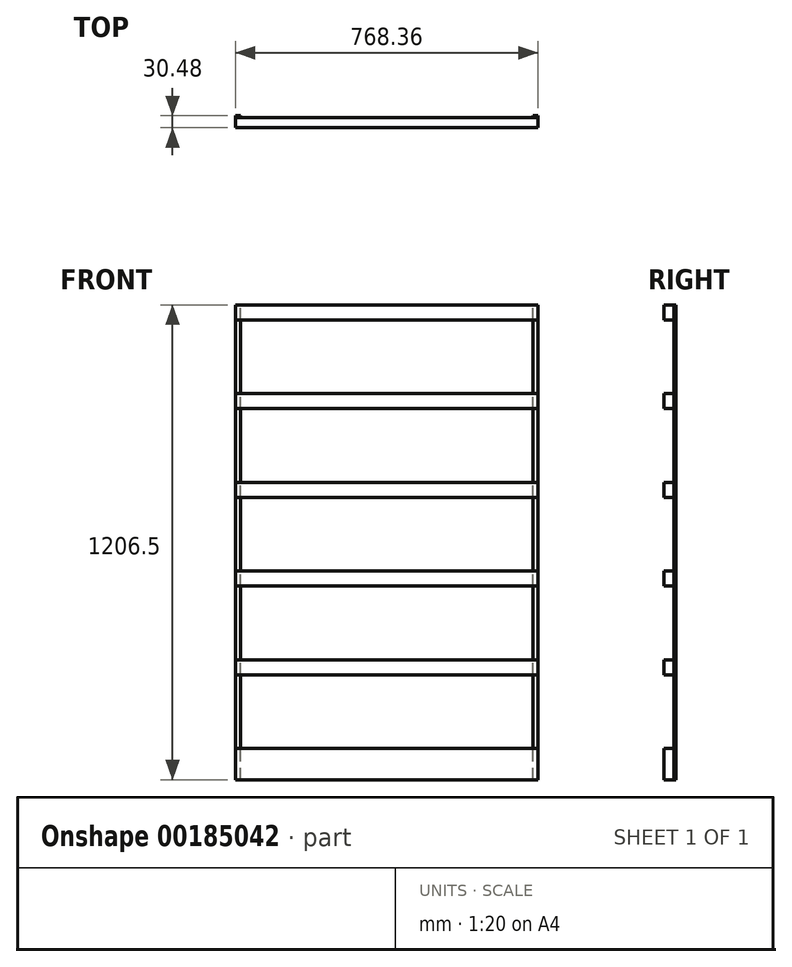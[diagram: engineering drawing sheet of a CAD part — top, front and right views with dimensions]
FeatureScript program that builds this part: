
annotation { "Feature Type Name" : "Feature", "Feature Type Description" : "" }
export const myFeature = defineFeature(function(context is Context, id is Id, definition is map)
    precondition{}
    {
        {
            var Q0;
            Q0=qCreatedBy(makeId("Front.planeOp"),FACE);
            var sketch = newSketch(context, id + "F0", { "sketchPlane" : qUnion([Q0])});
            skLineSegment(sketch, "E0.bottom", {"start": v(384.18, 603.25) * mm, "end": v(-384.18, 603.25) * mm});
            skLineSegment(sketch, "E0.top", {"start": v(384.18, -603.25) * mm, "end": v(-384.17, -603.25) * mm});
            skLineSegment(sketch, "E0.left", {"start": v(384.18, 603.25) * mm, "end": v(384.18, -603.25) * mm});
            skLineSegment(sketch, "E0.right", {"start": v(-384.18, 603.25) * mm, "end": v(-384.17, -603.25) * mm});
            skPoint(sketch, "E0.middle", {"position": v(0, 0) * mm});
            skSolve(sketch);
        }
        {
            var Q0;
            Q0 = qSketchRegion(id + "F0", true);
            extrude(context, id + "F1", {"entities" : qUnion([Q0]), "depth" : 25.4 * mm});
        }
        {
            var Q0;
            Q0=makeQuery(id+"F1.opExtrude","CAP_FACE",FACE,{"disambiguationData":[OSD([sQuery(id+"F0.wireOp",EDGE,"E0.bottom"),sQuery(id+"F0.wireOp",EDGE,"E0.top"),sQuery(id+"F0.wireOp",EDGE,"E0.left"),sQuery(id+"F0.wireOp",EDGE,"E0.right")])],"isStart":false});
            var sketch = newSketch(context, id + "F2", { "sketchPlane" : qUnion([Q0])});
            skLineSegment(sketch, "E1", {"start": v(-384.18, 565.15) * mm, "end": v(384.17, 565.15) * mm});
            skLineSegment(sketch, "E2", {"start": v(-384.18, 377.83) * mm, "end": v(384.18, 377.83) * mm});
            skLineSegment(sketch, "E3", {"start": v(-384.18, 339.73) * mm, "end": v(384.18, 339.73) * mm});
            skLineSegment(sketch, "E4", {"start": v(-384.18, 152.4) * mm, "end": v(384.18, 152.4) * mm});
            skLineSegment(sketch, "E5", {"start": v(-384.18, 114.3) * mm, "end": v(384.18, 114.3) * mm});
            skLineSegment(sketch, "E6", {"start": v(-384.18, -73.02) * mm, "end": v(384.18, -73.02) * mm});
            skLineSegment(sketch, "E7", {"start": v(-384.18, -111.12) * mm, "end": v(384.18, -111.12) * mm});
            skLineSegment(sketch, "E8", {"start": v(-384.17, -298.45) * mm, "end": v(384.18, -298.45) * mm});
            skLineSegment(sketch, "E9", {"start": v(-384.17, -336.55) * mm, "end": v(384.18, -336.55) * mm});
            skLineSegment(sketch, "E10", {"start": v(-384.17, -523.88) * mm, "end": v(384.18, -523.88) * mm});
            skLineSegment(sketch, "E11", {"start": v(-384.18, -336.55) * mm, "end": v(-384.17, -523.88) * mm});
            skLineSegment(sketch, "E12", {"start": v(384.18, -336.55) * mm, "end": v(384.18, -523.88) * mm});
            skLineSegment(sketch, "E13", {"start": v(384.18, -111.12) * mm, "end": v(384.18, -298.45) * mm});
            skLineSegment(sketch, "E14", {"start": v(-384.18, 565.15) * mm, "end": v(-384.18, 377.83) * mm});
            skLineSegment(sketch, "E15", {"start": v(384.17, 565.15) * mm, "end": v(384.18, 377.83) * mm});
            skLineSegment(sketch, "E16", {"start": v(384.18, 339.73) * mm, "end": v(384.18, 152.4) * mm});
            skLineSegment(sketch, "E17", {"start": v(-384.18, 339.73) * mm, "end": v(-384.18, 152.4) * mm});
            skLineSegment(sketch, "E18", {"start": v(-384.18, 114.3) * mm, "end": v(-384.18, -73.02) * mm});
            skSolve(sketch);
        }
        {
            var Q0;
            Q0 = qSketchRegion(id + "F2", true);
            var Q1;
            {var subQ0=sQuery(id+"F2.wireOp",EDGE,"E5");Q1=makeQuery(id+"F2.imprint","IMPRINT",FACE,{"disambiguationData":[TD([[makeQuery(id+"F2.imprint","IMPRINT",EDGE,{"derivedFrom":subQ0}),-1.0]])]});}
            var Q2;
            {var subQ0=sQuery(id+"F2.wireOp",EDGE,"E7");Q2=makeQuery(id+"F2.imprint","IMPRINT",FACE,{"disambiguationData":[TD([[makeQuery(id+"F2.imprint","IMPRINT",EDGE,{"derivedFrom":subQ0}),-1.0]])]});}
            extrude(context, id + "F3", {"entities" : qUnion([Q0, Q1, Q2]), "operationType" : NewBodyOperationType.REMOVE, "oppositeDirection" : true, "depth" : 25.4 * mm});
        }
        {
            var Q0;
            Q0=makeQuery(id+"F1.opExtrude","SWEPT_FACE",FACE,{"disambiguationData":[OSD([sQuery(id+"F0.wireOp",EDGE,"E0.bottom")])]});
            var sketch = newSketch(context, id + "F4", { "sketchPlane" : qUnion([Q0])});
            skLineSegment(sketch, "E19.bottom", {"start": v(-384.18, 0) * mm, "end": v(-371.48, 0) * mm});
            skLineSegment(sketch, "E19.top", {"start": v(-384.18, 5.08) * mm, "end": v(-371.48, 5.08) * mm});
            skLineSegment(sketch, "E19.left", {"start": v(-384.18, 0) * mm, "end": v(-384.18, 5.08) * mm});
            skLineSegment(sketch, "E19.right", {"start": v(-371.48, 0) * mm, "end": v(-371.48, 5.08) * mm});
            skLineSegment(sketch, "E20.bottom", {"start": v(384.18, 0) * mm, "end": v(371.48, 0) * mm});
            skLineSegment(sketch, "E20.top", {"start": v(384.18, 5.08) * mm, "end": v(371.48, 5.08) * mm});
            skLineSegment(sketch, "E20.left", {"start": v(384.18, 0) * mm, "end": v(384.18, 5.08) * mm});
            skLineSegment(sketch, "E20.right", {"start": v(371.48, 0) * mm, "end": v(371.48, 5.08) * mm});
            skSolve(sketch);
        }
        {
            var Q0;
            Q0 = qSketchRegion(id + "F4", true);
            var Q1;
            Q1=makeQuery(id+"F1.opExtrude","SWEPT_FACE",FACE,{"disambiguationData":[OSD([sQuery(id+"F0.wireOp",EDGE,"E0.top")])]});
            extrude(context, id + "F5", {"entities" : qUnion([Q0]), "endBound" : BoundingType.UP_TO_SURFACE, "oppositeDirection" : true, "endBoundEntityFace" : qUnion([Q1]), "depth" : 25.4 * mm});
        }
    });
